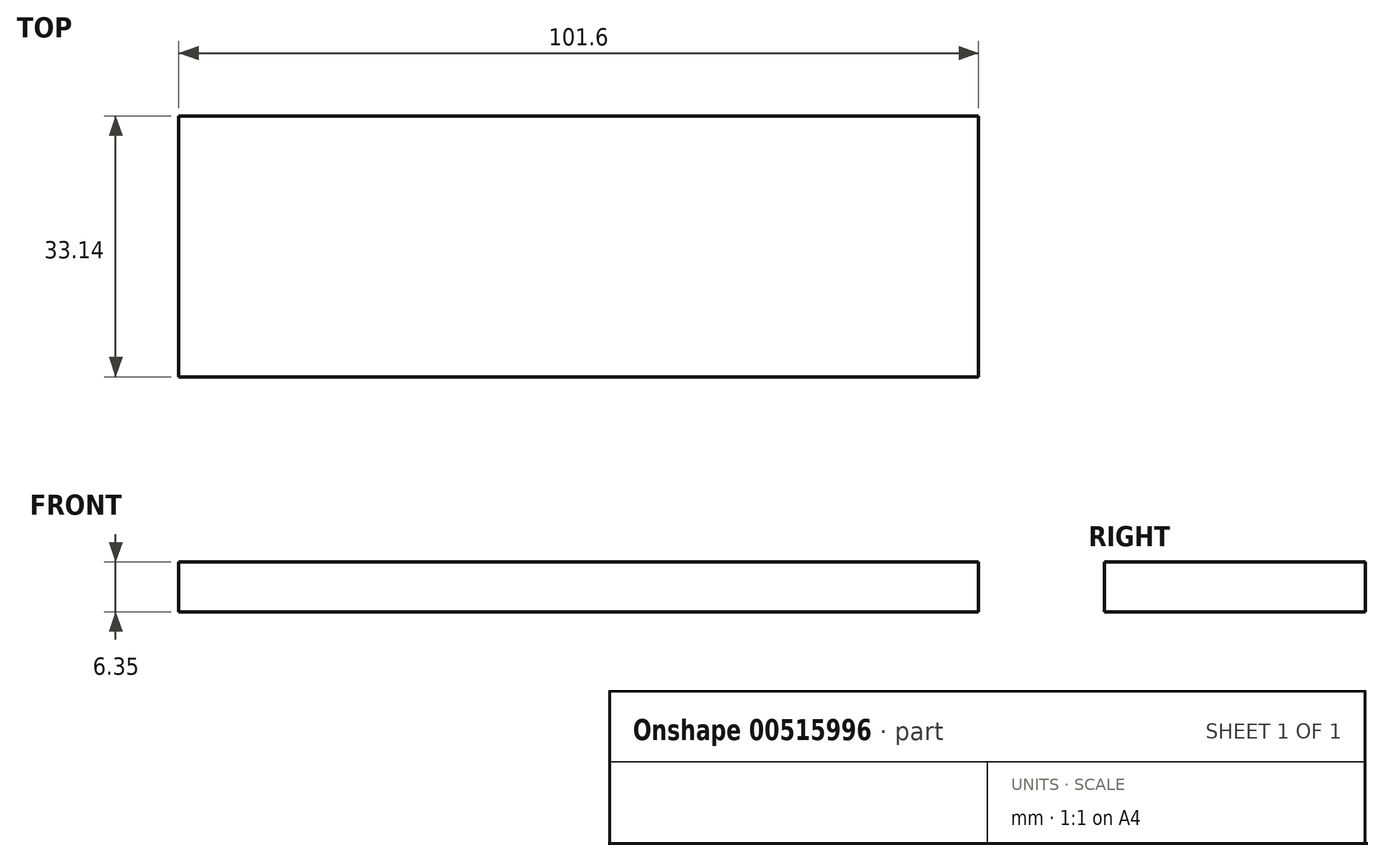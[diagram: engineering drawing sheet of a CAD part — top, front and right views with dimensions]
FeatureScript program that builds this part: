
annotation { "Feature Type Name" : "Feature", "Feature Type Description" : "" }
export const myFeature = defineFeature(function(context is Context, id is Id, definition is map)
    precondition{}
    {
        {
            var Q0;
            Q0=qCreatedBy(makeId("Top.planeOp"),FACE);
            var sketch = newSketch(context, id + "F0", { "sketchPlane" : qUnion([Q0])});
            skLineSegment(sketch, "E0.bottom", {"start": v(50.8, 16.57) * mm, "end": v(-50.8, 16.57) * mm});
            skLineSegment(sketch, "E0.top", {"start": v(50.8, -16.57) * mm, "end": v(-50.8, -16.57) * mm});
            skLineSegment(sketch, "E0.left", {"start": v(50.8, 16.57) * mm, "end": v(50.8, -16.57) * mm});
            skLineSegment(sketch, "E0.right", {"start": v(-50.8, 16.57) * mm, "end": v(-50.8, -16.57) * mm});
            skPoint(sketch, "E0.middle", {"position": v(0, 0) * mm});
            skSolve(sketch);
        }
        {
            var Q0;
            Q0=makeQuery(id+"F0.imprint","IMPRINT",FACE,{"disambiguationData":[TD([[makeQuery(id+"F0.imprint","IMPRINT",EDGE,{"derivedFrom":sQuery(id+"F0.wireOp",EDGE,"E0.bottom")}),1.0]])]});
            extrude(context, id + "F1", {"entities" : qUnion([Q0]), "depth" : 6.35 * mm, "offsetDistance" : 25.4 * mm});
        }
    });
